# Revit family: QF_ELECTROLUXPROFESSIONAL_589027_MCIBACEOAO
name_source: partatom
category: Specialty Equipment
revit_build: Autodesk Revit 2018 (Build: 20190510_1515(x64)
units: mm (PartAtom-declared; Revit-internal decimal feet)

## family parameters
Always vertical = Yes
Cut with Voids When Loaded = No
Part Type = Normal
Room Calculation Point = No
Round Connector Dimension = Use Diameter
Shared = No
Work Plane-Based = No

## types (1)
- QF_ELECTROLUXPROFESSIONAL_589027_MCIBACEOAO
    500 Pass Though Panel = Yes
    Conn Conduit = Yes
    Description = INDUCTION TOP,2 ZONES,2SIDE,500X900X250H
    Direct Waste Size = 0"
    Electrical Remarks = 400 V/3N ph/50/60 Hz
    HP = 13.4 HP
    Manufacturer = ELECTROLUX
    Max Overcurrent Protection = 0 A
    Min Ckt Ampacity = 0 A
    Model = 589027
    Phase = 3
    Volts = 400 V
    Watts = 10000 W
    Weight in Pounds = 55.1

## geometry (parser evidence)
native form markers: Blend x19, Sweep x8
no freeform markers — native parametric forms only
